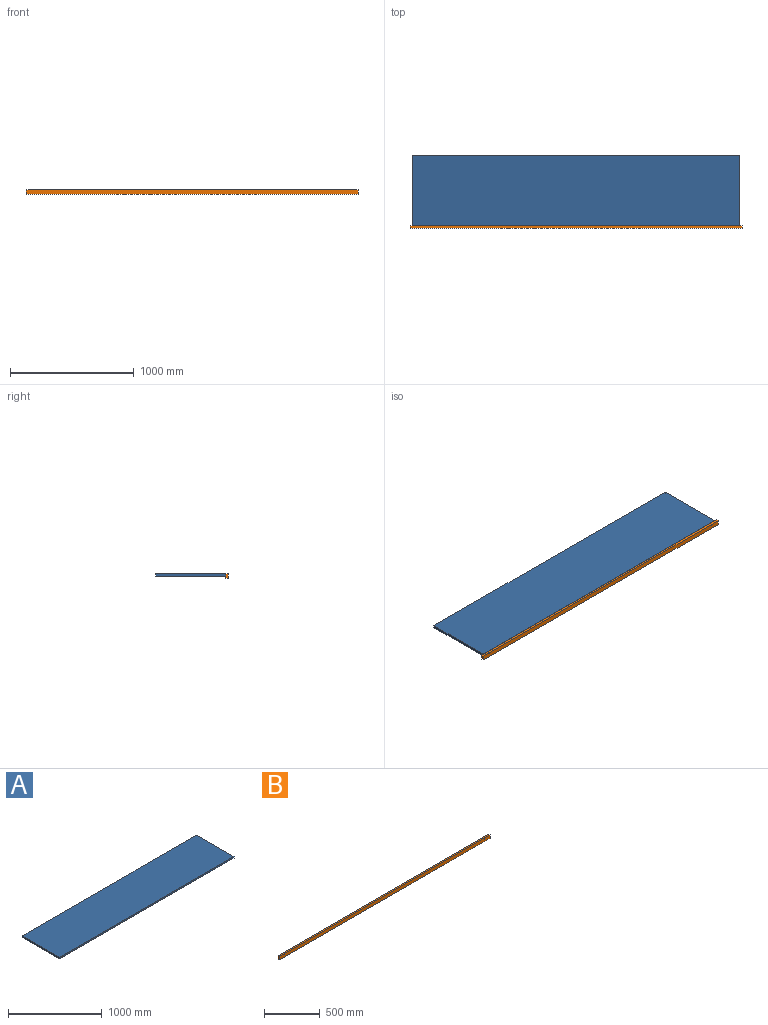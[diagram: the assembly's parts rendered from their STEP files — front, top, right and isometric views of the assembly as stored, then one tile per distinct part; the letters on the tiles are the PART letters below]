
ASSEMBLY  parts=2 mates=1
PART A: 12 faces, bbox 2641.6x565.2x19.1 mm
  f0: plane 565.15x19.05mm, normal (-1,0,0), area 10766.1mm2, adj f1,f3,f4,f5
  f1: plane 2641.6x19.05mm, normal (0,-1,0), area 50250.8mm2, adj f0,f2,f4,f5,f7,f9
  f2: plane 565.15x19.05mm, normal (1,0,0), area 10766.1mm2, adj f1,f3,f4,f5
  f3: plane 2641.6x19.05mm, normal (0,1,0), area 50322.5mm2, adj f0,f2,f4,f5
  f4: plane 2641.6x565.15mm, normal (0,0,1), area 1492900.2mm2, adj f0,f1,f2,f3
  f5: plane 2641.6x565.15mm, normal (0,0,-1), area 1492868.6mm2, adj f0,f1,f2,f3,f11
  f6: cone r=0mm half-angle=59deg, axis (0,-1,0), area 41.8mm2, adj f7
  f7: cylinder r=3.38mm len=12.7mm, axis (0,-1,0), area 269.6mm2, adj f1,f6
  f8: cone r=0mm half-angle=59deg, axis (0,-1,0), area 41.8mm2, adj f9
  f9: cylinder r=3.38mm len=12.7mm, axis (0,-1,0), area 269.6mm2, adj f1,f8
  f10: cone r=0mm half-angle=59deg, axis (0,0,-1), area 36.9mm2, adj f11
  f11: cylinder r=3.17mm len=12.7mm, axis (0,0,-1), area 253.4mm2, adj f5,f10
PART B: 10 faces, bbox 2679.7x19.1x38.1 mm
  f0: plane 38.1x19.08mm, normal (-1,0,0), area 726.8mm2, adj f1,f3,f4,f5
  f1: plane 2679.7x19.08mm, normal (0,0,-1), area 51116.3mm2, adj f0,f2,f4,f5
  f2: plane 38.1x19.08mm, normal (1,0,0), area 726.8mm2, adj f1,f3,f4,f5
  f3: plane 2679.7x19.08mm, normal (0,0,1), area 51116.3mm2, adj f0,f2,f4,f5
  f4: plane 2679.7x38.1mm, normal (0,-1,0), area 102096.6mm2, adj f0,f1,f2,f3
  f5: plane 2679.7x38.1mm, normal (0,1,0), area 102024.9mm2, adj f0,f1,f2,f3,f7,f9
  f6: cone r=0mm half-angle=59deg, axis (0,1,0), area 41.8mm2, adj f7
  f7: cylinder r=3.38mm len=12.7mm, axis (0,1,0), area 269.6mm2, adj f5,f6
  f8: cone r=0mm half-angle=59deg, axis (0,1,0), area 41.8mm2, adj f9
  f9: cylinder r=3.38mm len=12.7mm, axis (0,1,0), area 269.6mm2, adj f5,f8
PLACE A t=(-224.1,373.3,-65.97)mm
PLACE B t=(-243.15,373.3,-84.69)mm
MATE fastened B.f8 <-> A.f8  axis (0,1,0) through (-173.3,373.3,-56.44)mm
